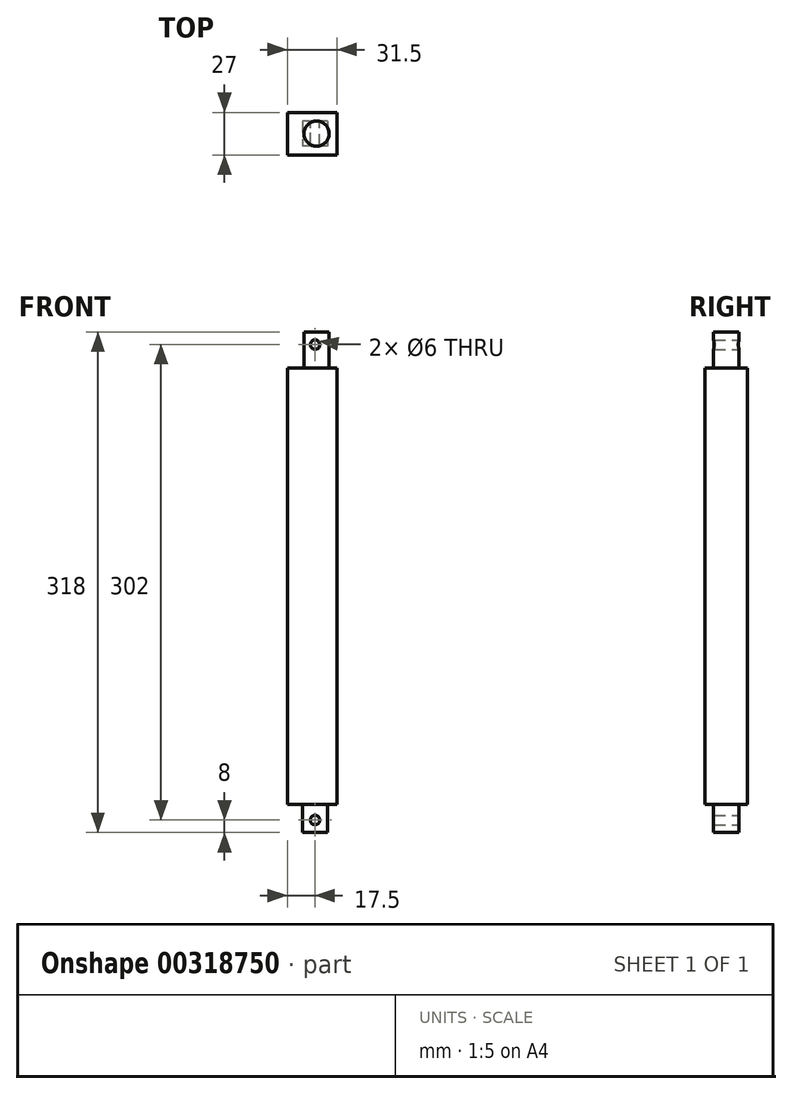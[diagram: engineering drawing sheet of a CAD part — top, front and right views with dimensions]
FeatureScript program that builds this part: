
annotation { "Feature Type Name" : "Feature", "Feature Type Description" : "" }
export const myFeature = defineFeature(function(context is Context, id is Id, definition is map)
    precondition{}
    {
        {
            var Q0;
            Q0=qCreatedBy(makeId("Top.planeOp"),FACE);
            var sketch = newSketch(context, id + "F0", { "sketchPlane" : qUnion([Q0])});
            skLineSegment(sketch, "E0.bottom", {"start": v(8, 8) * mm, "end": v(-8, 8) * mm});
            skLineSegment(sketch, "E0.top", {"start": v(8, -8) * mm, "end": v(-8, -8) * mm});
            skLineSegment(sketch, "E0.left", {"start": v(8, 8) * mm, "end": v(8, -8) * mm});
            skLineSegment(sketch, "E0.right", {"start": v(-8, 8) * mm, "end": v(-8, -8) * mm});
            skPoint(sketch, "E0.middle", {"position": v(0, 0) * mm});
            skSolve(sketch);
        }
        {
            var Q0;
            Q0=makeQuery(id+"F0.imprint","IMPRINT",FACE,{"disambiguationData":[TD([[makeQuery(id+"F0.imprint","IMPRINT",EDGE,{"derivedFrom":sQuery(id+"F0.wireOp",EDGE,"E0.bottom")}),1.0]])]});
            extrude(context, id + "F1", {"entities" : qUnion([Q0]), "depth" : 18 * mm, "offsetDistance" : 25 * mm});
        }
        {
            var Q0;
            Q0=makeQuery(id+"F1.opExtrude","CAP_FACE",FACE,{"disambiguationData":[OSD([sQuery(id+"F0.wireOp",EDGE,"E0.bottom"),sQuery(id+"F0.wireOp",EDGE,"E0.top"),sQuery(id+"F0.wireOp",EDGE,"E0.left"),sQuery(id+"F0.wireOp",EDGE,"E0.right")])],"isStart":false});
            var sketch = newSketch(context, id + "F2", { "sketchPlane" : qUnion([Q0])});
            skLineSegment(sketch, "E1.bottom", {"start": v(14, 13.5) * mm, "end": v(-17.5, 13.5) * mm});
            skLineSegment(sketch, "E1.top", {"start": v(14, -13.5) * mm, "end": v(-17.5, -13.5) * mm});
            skLineSegment(sketch, "E1.left", {"start": v(14, 13.5) * mm, "end": v(14, -13.5) * mm});
            skLineSegment(sketch, "E1.right", {"start": v(-17.5, 13.5) * mm, "end": v(-17.5, -13.5) * mm});
            skPoint(sketch, "E1.middle", {"position": v(-1.75, 0) * mm});
            skSolve(sketch);
        }
        {
            var Q0;
            Q0=makeQuery(id+"F2.imprint","IMPRINT",FACE,{"disambiguationData":[TD([[makeQuery(id+"F2.imprint","IMPRINT",EDGE,{"derivedFrom":sQuery(id+"F2.wireOp",EDGE,"E1.bottom")}),1.0]])]});
            var Q1;
            Q1=makeQuery(id+"F2.imprint","IMPRINT",FACE,{"disambiguationData":[TD([[makeQuery(id+"F2.imprint","IMPRINT",EDGE,{"derivedFrom":makeQuery(id+"F1.opExtrude","CAP_EDGE",EDGE,{"disambiguationData":[OSD([sQuery(id+"F0.wireOp",EDGE,"E0.bottom")])],"isStart":false})}),1.0]])]});
            extrude(context, id + "F3", {"entities" : qUnion([Q0, Q1]), "operationType" : NewBodyOperationType.ADD, "depth" : 277 * mm, "offsetDistance" : 25 * mm});
        }
        {
            var Q0;
            Q0=makeQuery(id+"F3.opExtrude","CAP_FACE",FACE,{"disambiguationData":[OSD([sQuery(id+"F2.wireOp",EDGE,"E1.bottom"),sQuery(id+"F2.wireOp",EDGE,"E1.top"),sQuery(id+"F2.wireOp",EDGE,"E1.left"),sQuery(id+"F2.wireOp",EDGE,"E1.right")])],"isStart":false});
            var sketch = newSketch(context, id + "F4", { "sketchPlane" : qUnion([Q0])});
            skCircle(sketch, "E2", {"center": v(1, 0) * mm, "radius": 8 * mm});
            skSolve(sketch);
        }
        {
            var Q0;
            Q0=makeQuery(id+"F4.imprint","IMPRINT",FACE,{"disambiguationData":[TD([[makeQuery(id+"F4.imprint","IMPRINT",EDGE,{"derivedFrom":sQuery(id+"F4.wireOp",EDGE,"E2")}),1.0]])]});
            extrude(context, id + "F5", {"entities" : qUnion([Q0]), "operationType" : NewBodyOperationType.ADD, "depth" : 23 * mm, "offsetDistance" : 25 * mm});
        }
        {
            var Q0;
            Q0=makeQuery(id+"F3.opExtrude","SWEPT_FACE",FACE,{"disambiguationData":[OSD([sQuery(id+"F2.wireOp",EDGE,"E1.bottom")])]});
            var sketch = newSketch(context, id + "F6", { "sketchPlane" : qUnion([Q0])});
            skCircle(sketch, "E3", {"center": v(0, 8) * mm, "radius": 3 * mm});
            skCircle(sketch, "E4", {"center": v(0, 310) * mm, "radius": 3 * mm});
            skPoint(sketch, "E5", {"position": v(0, 302.62) * mm});
            skSolve(sketch);
        }
        {
            var Q0;
            Q0 = qSketchRegion(id + "F6", true);
            extrude(context, id + "F7", {"entities" : qUnion([Q0]), "operationType" : NewBodyOperationType.REMOVE, "oppositeDirection" : true, "depth" : 25 * mm, "offsetDistance" : 25 * mm});
        }
    });
